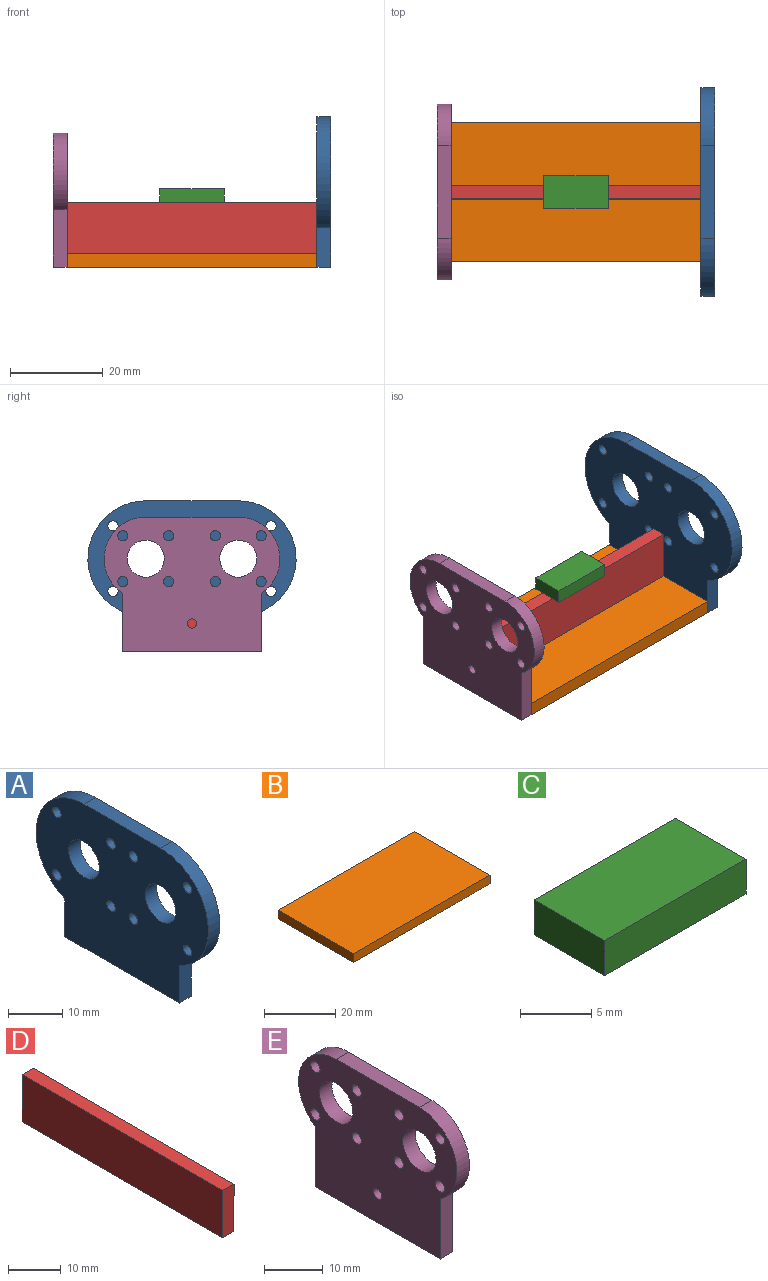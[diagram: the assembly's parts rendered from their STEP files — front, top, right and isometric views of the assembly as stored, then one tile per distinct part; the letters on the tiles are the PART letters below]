
ASSEMBLY  parts=5 mates=4
PART A: 18 faces, bbox 3x45x32.5 mm
  f0: cylinder r=12.5mm len=23.96mm, axis (1,0,0), area 102.4mm2, adj f1,f13,f16,f17
  f1: plane 8.54x3mm, normal (0,1,0), area 25.6mm2, adj f0,f2,f16,f17
  f2: plane 30x3mm, normal (0,0,-1), area 90mm2, adj f1,f3,f16,f17
  f3: plane 8.54x3mm, normal (0,-1,0), area 25.6mm2, adj f2,f4,f16,f17
  f4: cylinder r=12.5mm len=23.96mm, axis (1,0,0), area 102.4mm2, adj f3,f13,f16,f17
  f5: cylinder r=1.1mm len=3mm, axis (1,0,0), area 20.7mm2, adj f16,f17
  f6: cylinder r=1.1mm len=3mm, axis (1,0,0), area 20.7mm2, adj f16,f17
  f7: cylinder r=1.1mm len=3mm, axis (1,0,0), area 20.7mm2, adj f16,f17
  f8: cylinder r=1.1mm len=3mm, axis (1,0,0), area 20.7mm2, adj f16,f17
  f9: cylinder r=1.1mm len=3mm, axis (1,0,0), area 20.7mm2, adj f16,f17
  f10: cylinder r=1.1mm len=3mm, axis (1,0,0), area 20.7mm2, adj f16,f17
  f11: cylinder r=1.1mm len=3mm, axis (1,0,0), area 20.7mm2, adj f16,f17
  f12: cylinder r=1.1mm len=3mm, axis (1,0,0), area 20.7mm2, adj f16,f17
  f13: plane 20x3mm, normal (0,0,1), area 60mm2, adj f0,f4,f16,f17
  f14: cylinder r=4mm len=8mm, axis (1,0,0), area 75.4mm2, adj f16,f17
  f15: cylinder r=4mm len=8mm, axis (1,0,0), area 75.4mm2, adj f16,f17
  f16: plane 45x32.5mm, normal (-1,0,0), area 1088.4mm2, adj f0,f1,f2,f3,f4,f5,f6,f7
  f17: plane 45x32.5mm, normal (1,0,0), area 1088.4mm2, adj f0,f1,f2,f3,f4,f5,f6,f7
PART B: 6 faces, bbox 54x30x3 mm
  f0: plane 30x3mm, normal (1,0,0), area 90mm2, adj f1,f3,f4,f5
  f1: plane 54x3mm, normal (0,-1,0), area 162mm2, adj f0,f2,f4,f5
  f2: plane 30x3mm, normal (-1,0,0), area 90mm2, adj f1,f3,f4,f5
  f3: plane 54x3mm, normal (0,1,0), area 162mm2, adj f0,f2,f4,f5
  f4: plane 54x30mm, normal (0,0,-1), area 1620mm2, adj f0,f1,f2,f3
  f5: plane 54x30mm, normal (0,0,1), area 1620mm2, adj f0,f1,f2,f3
PART C: 6 faces, bbox 14x7x3 mm
  f0: plane 7x3mm, normal (1,0,0), area 21mm2, adj f1,f3,f4,f5
  f1: plane 14x3mm, normal (0,-1,0), area 42mm2, adj f0,f2,f4,f5
  f2: plane 7x3mm, normal (-1,0,0), area 21mm2, adj f1,f3,f4,f5
  f3: plane 14x3mm, normal (0,1,0), area 42mm2, adj f0,f2,f4,f5
  f4: plane 14x7mm, normal (0,0,-1), area 98mm2, adj f0,f1,f2,f3
  f5: plane 14x7mm, normal (0,0,1), area 98mm2, adj f0,f1,f2,f3
PART D: 6 faces, bbox 3x54x11 mm
  f0: plane 11x3mm, normal (0,1,0), area 33mm2, adj f1,f3,f4,f5
  f1: plane 54x3mm, normal (0,0,-1), area 162mm2, adj f0,f2,f4,f5
  f2: plane 11x3mm, normal (0,-1,0), area 33mm2, adj f1,f3,f4,f5
  f3: plane 54x3mm, normal (0,0,1), area 162mm2, adj f0,f2,f4,f5
  f4: plane 54x11mm, normal (-1,0,0), area 594mm2, adj f0,f1,f2,f3
  f5: plane 54x11mm, normal (1,0,0), area 594mm2, adj f0,f1,f2,f3
PART E: 19 faces, bbox 3x38x29 mm
  f0: cylinder r=9mm len=16.48mm, axis (1,0,0), area 68.9mm2, adj f1,f14,f17,f18
  f1: plane 12.52x3mm, normal (0,1,0), area 37.6mm2, adj f0,f2,f17,f18
  f2: plane 30x3mm, normal (0,0,-1), area 90mm2, adj f1,f3,f17,f18
  f3: plane 12.52x3mm, normal (0,-1,0), area 37.6mm2, adj f2,f4,f17,f18
  f4: cylinder r=9mm len=16.48mm, axis (1,0,0), area 68.9mm2, adj f3,f14,f17,f18
  f5: cylinder r=1mm len=3mm, axis (1,0,0), area 18.8mm2, adj f17,f18
  f6: cylinder r=1.1mm len=3mm, axis (1,0,0), area 20.7mm2, adj f17,f18
  f7: cylinder r=1.1mm len=3mm, axis (1,0,0), area 20.7mm2, adj f17,f18
  f8: cylinder r=1.1mm len=3mm, axis (1,0,0), area 20.7mm2, adj f17,f18
  f9: cylinder r=1.1mm len=3mm, axis (1,0,0), area 20.7mm2, adj f17,f18
  f10: cylinder r=1.1mm len=3mm, axis (1,0,0), area 20.7mm2, adj f17,f18
  f11: cylinder r=1.1mm len=3mm, axis (1,0,0), area 20.7mm2, adj f17,f18
  f12: cylinder r=1.1mm len=3mm, axis (1,0,0), area 20.7mm2, adj f17,f18
  f13: cylinder r=1.1mm len=3mm, axis (1,0,0), area 20.7mm2, adj f17,f18
  f14: plane 20x3mm, normal (0,0,1), area 60mm2, adj f0,f4,f17,f18
  f15: cylinder r=4mm len=8mm, axis (1,0,0), area 75.4mm2, adj f17,f18
  f16: cylinder r=4mm len=8mm, axis (1,0,0), area 75.4mm2, adj f17,f18
  f17: plane 38x29mm, normal (-1,0,0), area 815.3mm2, adj f0,f1,f2,f3,f4,f5,f6,f7
  f18: plane 38x29mm, normal (1,0,0), area 815.3mm2, adj f0,f1,f2,f3,f4,f5,f6,f7
PLACE A t=(43.32,-5.11,24.66)mm
PLACE B t=(-10.68,-10.11,4.66)mm
PLACE C t=(9.32,1.39,18.66)mm
PLACE D rot(axis=(0,0,-1),90deg) t=(-10.68,6.39,7.66)mm
PLACE E t=(-13.68,-5.11,24.66)mm
MATE fastened D.f3 <-> C.f4  axis (0,0,1) through (16.32,4.89,18.66)mm
MATE fastened E.f18 <-> B.f2  axis (1,0,0) through (-10.68,4.89,4.66)mm
MATE fastened B.f5 <-> D.f1  axis (0,0,1) through (16.32,4.89,7.66)mm
MATE fastened B.f0 <-> A.f16  axis (1,0,0) through (43.32,4.89,4.66)mm
